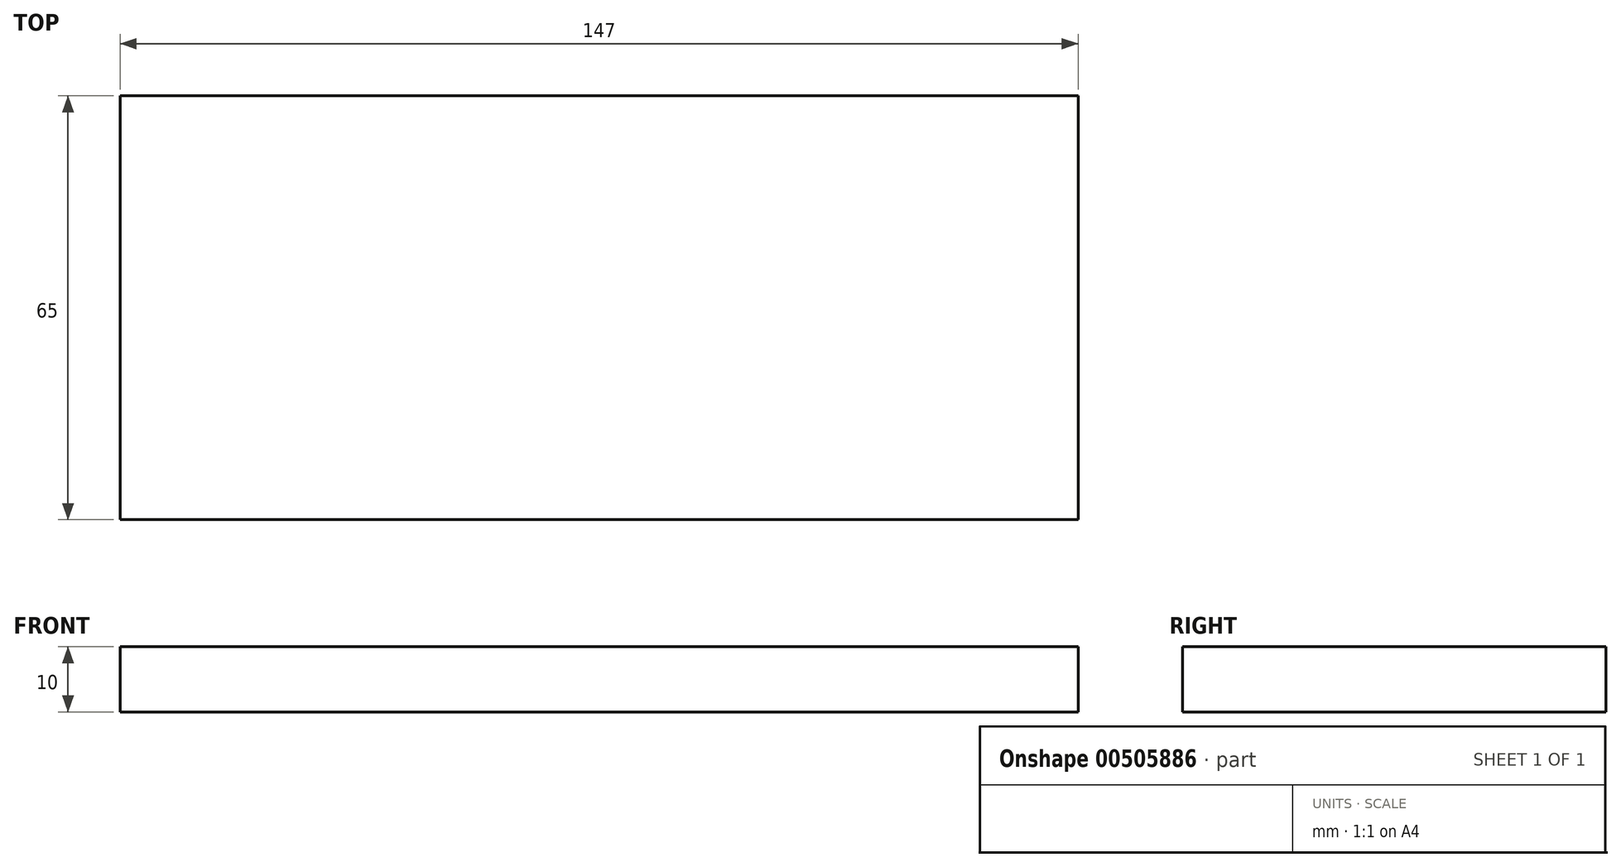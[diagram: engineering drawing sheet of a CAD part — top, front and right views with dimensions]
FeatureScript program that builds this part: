
annotation { "Feature Type Name" : "Feature", "Feature Type Description" : "" }
export const myFeature = defineFeature(function(context is Context, id is Id, definition is map)
    precondition{}
    {
        {
            var Q0;
            Q0=qCreatedBy(makeId("Top.planeOp"),FACE);
            var sketch = newSketch(context, id + "F0", { "sketchPlane" : qUnion([Q0])});
            skLineSegment(sketch, "E0.bottom", {"start": v(-73.5, 32.5) * mm, "end": v(73.5, 32.5) * mm});
            skLineSegment(sketch, "E0.top", {"start": v(-73.5, -32.5) * mm, "end": v(73.5, -32.5) * mm});
            skLineSegment(sketch, "E0.left", {"start": v(-73.5, 32.5) * mm, "end": v(-73.5, -32.5) * mm});
            skLineSegment(sketch, "E0.right", {"start": v(73.5, 32.5) * mm, "end": v(73.5, -32.5) * mm});
            skPoint(sketch, "E0.middle", {"position": v(0, 0) * mm});
            skSolve(sketch);
        }
        {
            var Q0;
            Q0=makeQuery(id+"F0.imprint","IMPRINT",FACE,{"disambiguationData":[TD([[makeQuery(id+"F0.imprint","IMPRINT",EDGE,{"derivedFrom":sQuery(id+"F0.wireOp",EDGE,"E0.bottom")}),-1.0]])]});
            extrude(context, id + "F1", {"entities" : qUnion([Q0]), "depth" : 10 * mm});
        }
    });
